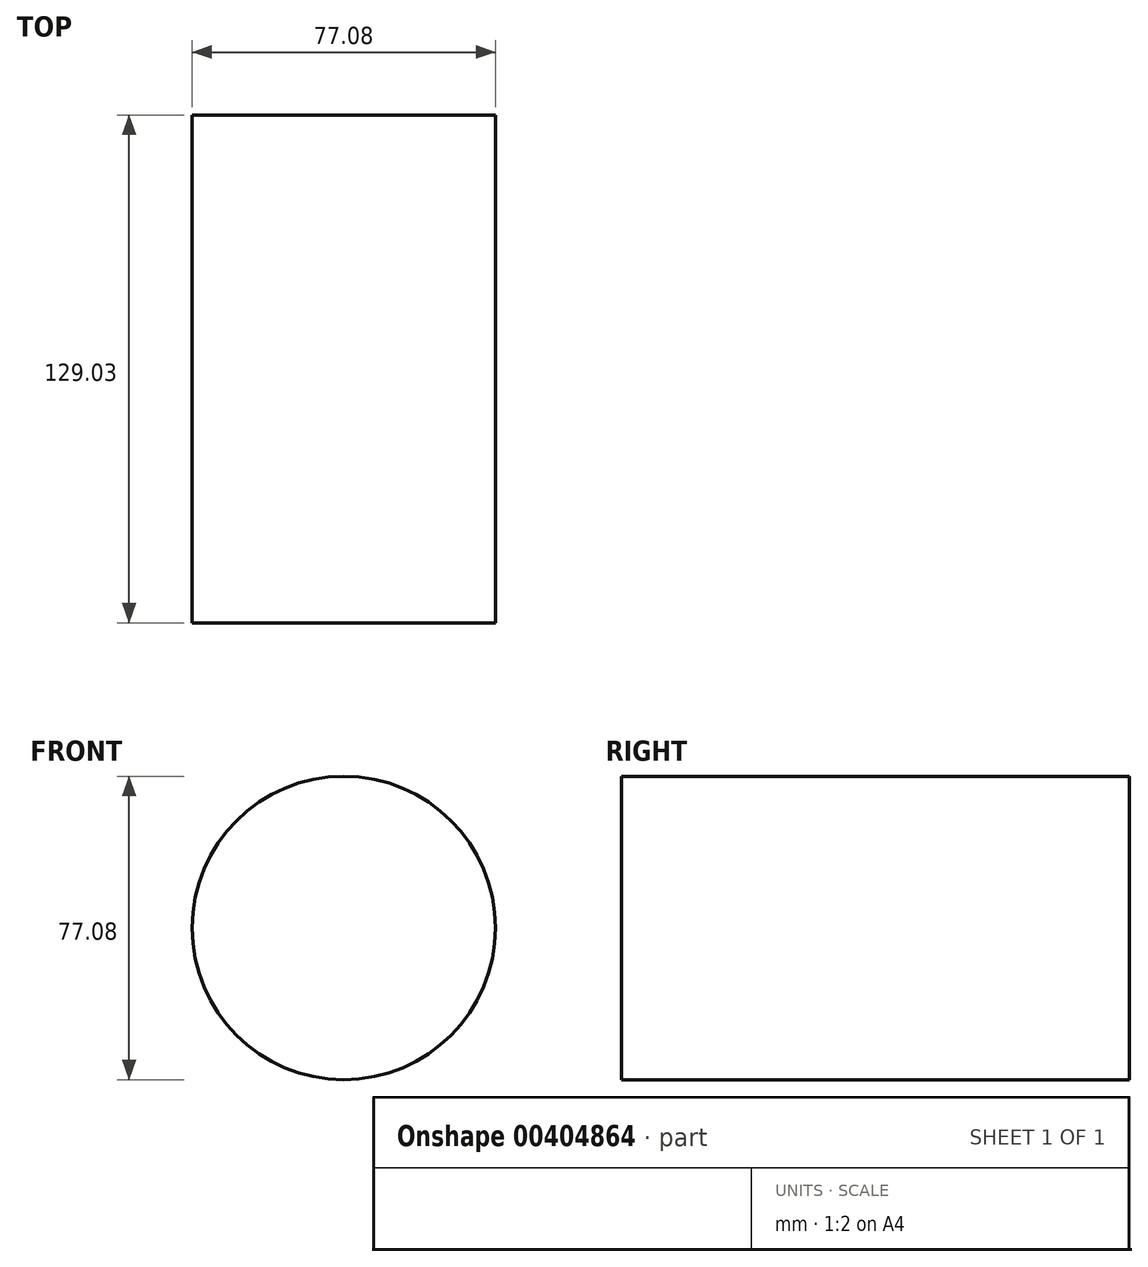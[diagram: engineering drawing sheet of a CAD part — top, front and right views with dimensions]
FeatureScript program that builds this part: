
annotation { "Feature Type Name" : "Feature", "Feature Type Description" : "" }
export const myFeature = defineFeature(function(context is Context, id is Id, definition is map)
    precondition{}
    {
        {
            var Q0;
            Q0=qCreatedBy(makeId("Front.planeOp"),FACE);
            var sketch = newSketch(context, id + "F0", { "sketchPlane" : qUnion([Q0])});
            skCircle(sketch, "E0", {"center": v(0, 0) * mm, "radius": 38.54 * mm});
            skSolve(sketch);
        }
        {
            var Q0;
            Q0 = qSketchRegion(id + "F0", true);
            extrude(context, id + "F1", {"entities" : qUnion([Q0]), "oppositeDirection" : true, "depth" : 129.03 * mm});
        }
    });
